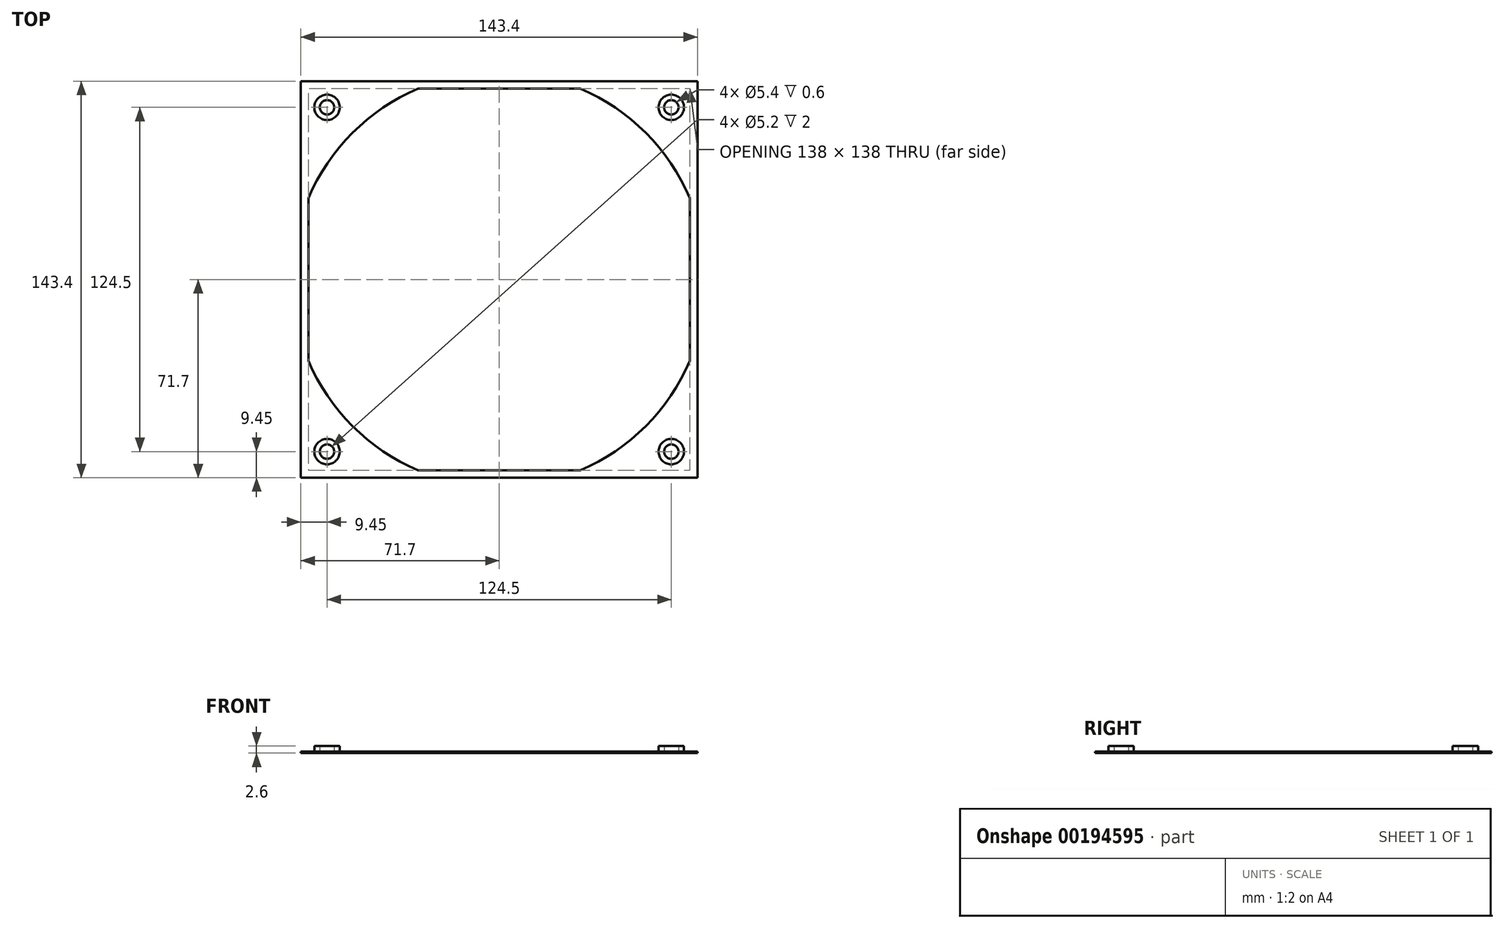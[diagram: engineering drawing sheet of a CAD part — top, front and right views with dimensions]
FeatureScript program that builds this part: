
annotation { "Feature Type Name" : "Feature", "Feature Type Description" : "" }
export const myFeature = defineFeature(function(context is Context, id is Id, definition is map)
    precondition{}
    {
        {
            var Q0;
            Q0=qCreatedBy(makeId("Top.planeOp"),FACE);
            var sketch = newSketch(context, id + "F0", { "sketchPlane" : qUnion([Q0])});
            skLineSegment(sketch, "E0.bottom", {"start": v(70.5, 70.5) * mm, "end": v(-70.5, 70.5) * mm, "construction": true});
            skLineSegment(sketch, "E0.top", {"start": v(70.5, -70.5) * mm, "end": v(-70.5, -70.5) * mm, "construction": true});
            skLineSegment(sketch, "E0.left", {"start": v(70.5, 70.5) * mm, "end": v(70.5, -70.5) * mm, "construction": true});
            skLineSegment(sketch, "E0.right", {"start": v(-70.5, 70.5) * mm, "end": v(-70.5, -70.5) * mm, "construction": true});
            skPoint(sketch, "E0.middle", {"position": v(0, 0) * mm});
            skLineSegment(sketch, "E1.bottom", {"start": v(62.25, 62.25) * mm, "end": v(-62.25, 62.25) * mm, "construction": true});
            skLineSegment(sketch, "E1.top", {"start": v(62.25, -62.25) * mm, "end": v(-62.25, -62.25) * mm, "construction": true});
            skLineSegment(sketch, "E1.left", {"start": v(62.25, 62.25) * mm, "end": v(62.25, -62.25) * mm, "construction": true});
            skLineSegment(sketch, "E1.right", {"start": v(-62.25, 62.25) * mm, "end": v(-62.25, -62.25) * mm, "construction": true});
            skLineSegment(sketch, "E2.bottom", {"start": v(69, 69) * mm, "end": v(-69, 69) * mm, "construction": true});
            skLineSegment(sketch, "E2.top", {"start": v(69, -69) * mm, "end": v(-69, -69) * mm, "construction": true});
            skLineSegment(sketch, "E2.left", {"start": v(69, 69) * mm, "end": v(69, -69) * mm, "construction": true});
            skLineSegment(sketch, "E2.right", {"start": v(-69, 69) * mm, "end": v(-69, -69) * mm, "construction": true});
            skArc(sketch, "E3", {"start": v(29.4, 69) * mm, "mid": v(53.03, 53.03) * mm, "end": v(69, 29.4) * mm, "construction": true});
            skArc(sketch, "E4", {"start": v(-29.4, 69) * mm, "mid": v(-53.03, 53.03) * mm, "end": v(-69, 29.4) * mm, "construction": true});
            skArc(sketch, "E5", {"start": v(-69, -29.4) * mm, "mid": v(-53.03, -53.03) * mm, "end": v(-29.4, -69) * mm, "construction": true});
            skArc(sketch, "E6", {"start": v(69, -29.4) * mm, "mid": v(53.03, -53.03) * mm, "end": v(29.4, -69) * mm, "construction": true});
            skCircle(sketch, "E7", {"center": v(-62.25, 62.25) * mm, "radius": 2.6 * mm, "construction": true});
            skCircle(sketch, "E8", {"center": v(62.25, 62.25) * mm, "radius": 2.6 * mm, "construction": true});
            skCircle(sketch, "E9", {"center": v(-62.25, -62.25) * mm, "radius": 2.6 * mm, "construction": true});
            skCircle(sketch, "E10", {"center": v(62.25, -62.25) * mm, "radius": 2.6 * mm, "construction": true});
            skSolve(sketch);
        }
        {
            var Q0;
            Q0=qCreatedBy(makeId("Top.planeOp"),FACE);
            var sketch = newSketch(context, id + "F1", { "sketchPlane" : qUnion([Q0])});
            skLineSegment(sketch, "E11.0", {"start": v(70.5, 70.5) * mm, "end": v(-70.5, 70.5) * mm, "construction": true});
            skLineSegment(sketch, "E12.0", {"start": v(-70.5, 70.5) * mm, "end": v(-70.5, -70.5) * mm, "construction": true});
            skLineSegment(sketch, "E13.0", {"start": v(70.5, -70.5) * mm, "end": v(-70.5, -70.5) * mm, "construction": true});
            skLineSegment(sketch, "E14.0", {"start": v(70.5, 70.5) * mm, "end": v(70.5, -70.5) * mm, "construction": true});
            skLineSegment(sketch, "E15.0", {"start": v(71.7, 71.7) * mm, "end": v(-71.7, 71.7) * mm});
            skLineSegment(sketch, "E15.1", {"start": v(71.7, 71.7) * mm, "end": v(71.7, -71.7) * mm});
            skLineSegment(sketch, "E15.2", {"start": v(71.7, -71.7) * mm, "end": v(-71.7, -71.7) * mm});
            skLineSegment(sketch, "E15.3", {"start": v(-71.7, 71.7) * mm, "end": v(-71.7, -71.7) * mm});
            skArc(sketch, "E16.0", {"start": v(-29.4, 69) * mm, "mid": v(-53.03, 53.03) * mm, "end": v(-69, 29.4) * mm});
            skArc(sketch, "E17.0", {"start": v(29.4, 69) * mm, "mid": v(53.03, 53.03) * mm, "end": v(69, 29.4) * mm});
            skArc(sketch, "E18.0", {"start": v(69, -29.4) * mm, "mid": v(53.03, -53.03) * mm, "end": v(29.4, -69) * mm});
            skArc(sketch, "E19.0", {"start": v(-69, -29.4) * mm, "mid": v(-53.03, -53.03) * mm, "end": v(-29.4, -69) * mm});
            skLineSegment(sketch, "E20", {"start": v(-29.4, 69) * mm, "end": v(29.4, 69) * mm});
            skLineSegment(sketch, "E21", {"start": v(69, 29.4) * mm, "end": v(69, -29.4) * mm});
            skLineSegment(sketch, "E22", {"start": v(-69, 29.4) * mm, "end": v(-69, -29.4) * mm});
            skLineSegment(sketch, "E23", {"start": v(-29.4, -69) * mm, "end": v(29.4, -69) * mm});
            skSolve(sketch);
        }
        {
            var Q0;
            Q0=qCreatedBy(makeId("Top.planeOp"),FACE);
            var sketch = newSketch(context, id + "F2", { "sketchPlane" : qUnion([Q0])});
            skCircle(sketch, "E24.0", {"center": v(-62.25, 62.25) * mm, "radius": 2.6 * mm, "construction": true});
            skCircle(sketch, "E25.0", {"center": v(62.25, 62.25) * mm, "radius": 2.6 * mm, "construction": true});
            skCircle(sketch, "E26.0", {"center": v(62.25, -62.25) * mm, "radius": 2.6 * mm, "construction": true});
            skCircle(sketch, "E27.0", {"center": v(-62.25, -62.25) * mm, "radius": 2.6 * mm, "construction": true});
            skCircle(sketch, "E28.0", {"center": v(62.25, 62.25) * mm, "radius": 2.7 * mm});
            skCircle(sketch, "E29.0", {"center": v(-62.25, 62.25) * mm, "radius": 2.7 * mm});
            skCircle(sketch, "E30.0", {"center": v(-62.25, -62.25) * mm, "radius": 2.7 * mm});
            skCircle(sketch, "E31.0", {"center": v(62.25, -62.25) * mm, "radius": 2.7 * mm});
            skSolve(sketch);
        }
        {
            var Q0;
            Q0=qSketchRegion(id+"F1",true);
            extrude(context, id + "F3", {"entities" : qUnion([Q0]), "oppositeDirection" : true, "depth" : 0.6 * mm});
        }
        {
            var Q0;
            Q0=qSketchRegion(id+"F2",true);
            extrude(context, id + "F4", {"entities" : qUnion([Q0]), "operationType" : NewBodyOperationType.REMOVE, "endBound" : BoundingType.THROUGH_ALL, "oppositeDirection" : true, "depth" : 25 * mm});
        }
        {
            var Q0;
            Q0=qCreatedBy(makeId("Top.planeOp"),FACE);
            var sketch = newSketch(context, id + "F5", { "sketchPlane" : qUnion([Q0])});
            skCircle(sketch, "E32.0", {"center": v(-62.25, 62.25) * mm, "radius": 2.6 * mm});
            skCircle(sketch, "E33.0", {"center": v(62.25, 62.25) * mm, "radius": 2.6 * mm});
            skCircle(sketch, "E34.0", {"center": v(62.25, -62.25) * mm, "radius": 2.6 * mm});
            skCircle(sketch, "E35.0", {"center": v(-62.25, -62.25) * mm, "radius": 2.6 * mm});
            skCircle(sketch, "E36.0", {"center": v(-62.25, 62.25) * mm, "radius": 4.6 * mm});
            skCircle(sketch, "E37.1.0", {"center": v(-62.25, -62.25) * mm, "radius": 4.6 * mm});
            skCircle(sketch, "E37.2.0", {"center": v(62.25, -62.25) * mm, "radius": 4.6 * mm});
            skCircle(sketch, "E37.3.0", {"center": v(62.25, 62.25) * mm, "radius": 4.6 * mm});
            skPoint(sketch, "E37.center", {"position": v(0, 0) * mm});
            skSolve(sketch);
        }
        {
            var Q0;
            Q0 = qSketchRegion(id + "F5", true);
            extrude(context, id + "F6", {"entities" : qUnion([Q0]), "operationType" : NewBodyOperationType.ADD, "depth" : 2 * mm});
        }
    });
